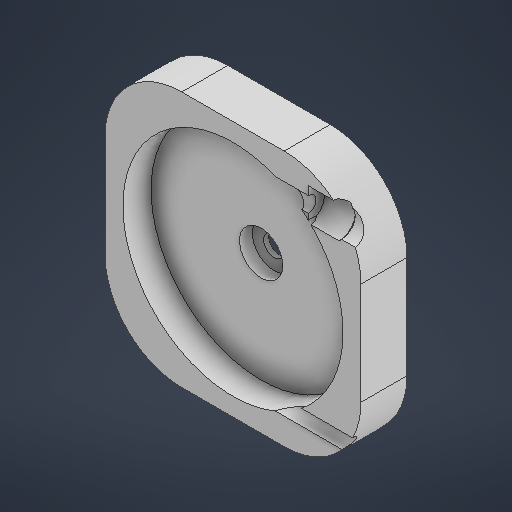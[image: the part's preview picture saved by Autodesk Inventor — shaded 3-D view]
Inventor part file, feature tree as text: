
AUTODESK INVENTOR PART (.ipt)
format: ipt  version: 2025.3 (Build 293356030, 356C)  size: 272,896 bytes
history: native  units: mm
features: extrude x3, sketch x2, revolve x2
ambient origin geometry x8: Origin, YZ Plane, XZ Plane, XY Plane, X Axis, Y Axis, Z Axis, Center Point
bodies: Solid1 (feature_tree)
feature tree (7):
  sketch  "Sketch1"  dims[d0=100.0mm d1=86.0mm]
  extrude  "Extrusion1"  Depth=86.0mm
  extrude  "Extrusion2"  Depth=18.0mm
  extrude  "Extrusion3"  Depth=18.0mm TaperAngle=0.0deg
  sketch  "Sketch3"  dims[d2=16.9mm d3=8.0mm d4=2.0mm d5=0.0mm d6=7.0mm d7=0.0mm d8=18.0mm d9=0.0mm d10=30.0mm d12=10.65mm d13=14.65mm d14=12.65mm d15=45.0deg d16=45.0deg d17=15.0mm d18=6.0mm d19=12.0mm d20=360.0deg d21=7.0mm d22=6.0mm d24=90.0deg d25=0.872665mm]
  revolve  "Revolution1"  [1 undecoded]
  revolve  "Revolution2"  [1 undecoded]
note: 2 required parameter values undecoded (feature->parameter linkage not recoverable at this tier; creation-order binding heuristic only, values carry confidence <= 0.55)
